# Revit family: QF_Vivreau_Vi2H
name_source: partatom
category: Specialty Equipment
revit_build: Autodesk Revit 2018 (Build: 20190510_1515(x64)
units: mm (PartAtom-declared; Revit-internal decimal feet)

## family parameters
Always vertical = Yes
Cut with Voids When Loaded = No
OmniClass Number = 23.40.40.14.24
OmniClass Title = Food Dispensing Equipment
Part Type = Normal
Room Calculation Point = No
Round Connector Dimension = Use Diameter
Shared = No
Work Plane-Based = No

## types (1)
- QF_Vivreau_Vi2H
    2nd Apparent Power = 1320 VA
    2nd FL Amps = 11 A
    2nd Number of Poles = 1
    2nd Phase = 1
    2nd Volts = 120 V
    Apparent Power = 1560 VA
    Assembly Code = E1090320
    BTUH = 0.0 Btu/h
    CSI MasterFormat = 11 46 00
    Cabinet Height = 2' - 6"
    Cabinet Width = 2' - 6"
    Cold Water Connection Height = 2' - 0"
    Cold Water Flow = 1 GPM
    Cold Water Maximum Pressure = 90.00 psi
    Cold Water Minimum Pressure = 50.00 psi
    Cold Water RI Height = 0' - 0"
    Cold Water Size = 1"
    Cold Water Temperature Recommended = 60 °F
    Conn Conduit = No
    Conn Plug = 5-20P
    Cycle = 60 Hz
    Description = Water Dispenser
    Elec Conn Connection Height = 2' - 0"
    Elec Conn RI Height = 0' - 0"
    Electric Connection Type = Plug
    Electrical Remarks = Requires Two (2) Electrical Connections, One At 120V/60/1 13 Amps (NEMA 5-20R), One At 120V/60/1 11 Amps (NEMA 5-20R) GFCI Recommended
    FL Amps = 13 A
    Foodservice Equipment Identifier = Yes
    Identify Quantity as Lot = Yes
    Indirect Waste Connection Type = Vertical Stand Pipe
    Indirect Waste Flow = 0 GPM
    Indirect Waste Size = 1"
    Manufacturer = Vivreau
    Masterspec = Division 11
    Max Overcurrent Protection = 18 A
    Min Ckt Ampacity = 13 A
    Model = Vi2H
    Number of Poles = 1
    Phase = 1
    Plumbing Connection Type = FNPT Ball Valve
    Plumbing Remarks = Cold Water To Be Tee'ed Off to Each Filter, Cold Water Consumption Will Vary Based On Use, Indirect Waste Flow Willl Vary Based On Use
    Refrigerant Type = 134a
    Refrigerant Volume = 0.000220 kip
    Specification by Manufacturer = Vivreau Water Dispensing System, single tap, fully-integrated undercounter, advanced micro-filtered, chilled still & sparkling drinking water, 11 liters/hour flow for instant hot water, touch control dispenser with hot water safety feature, cooler/carbonator, water filter, descaling filter, zero splash, anti-flood detection, removable dispense nozzle, CO2 cylinder (CO2 is customer supplied), component format, x2 20amp electrical receptacle (5-20R) 120v, 60Hz (13 amps & 11 amps), ETL, NSF (30"W x 24"D x 30"H cabinet required for installation, for indoor use only)
    URL = https://vivreauwater.com
    URL Cutsheet = https://vivreauwater.com
    Volts = 120 V
    Waste Water Discharge Temperature = 0 °F
    Watts = 1560 W
    Weight in Pounds = 140

## geometry (parser evidence)
native form markers: Sweep x23
no freeform markers — native parametric forms only
